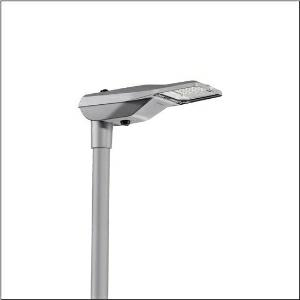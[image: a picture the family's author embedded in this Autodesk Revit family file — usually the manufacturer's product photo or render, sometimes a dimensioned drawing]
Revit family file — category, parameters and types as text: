
# Revit family: streetlight_sl_21_iq_micro___st1_0a_5xe1d31y08db_0307
name_source: partatom
category: Lighting Fixtures
units: mm (PartAtom-declared; Revit-internal decimal feet)

## family parameters
Cut with Voids When Loaded = No
Host = Face
Light Source = No
Part Type = Normal
Room Calculation Point = No
Round Connector Dimension = Use Diameter
Shared = No

## types (1)
- --- (1 x LED, 5110 lm, 39.1 W, 3000K)
    Apparent Load = 39 VA
    CIE Flux Codes = 37 72 97 100 100
    Color Rendering = 70
    Color Temperature = 3000K
    Default Elevation = 1800 mm
    Description = Streetlight SL 21 iQ micro, mast luminaire, primary light control with lens, of PMMA, primary optical cover: cover, of toughened safety glass, transparent, light distribution: ST1.0a, light emission: direct distribution, primary light characteristic: asymmetric, installation type: post-top, side-entry, LED, High Power LED, rated luminous flux: 5.110lm, luminous efficacy: 131lm/W, light colour: 730, colour temperature: 3000K, control gear: iQ-Street Remote, D4i with power reduction, control: pre-setting: logarithmic dimming characteristic, Street-Remote, Auto-Match, Temp-Guard, Lumen-Switch, Night-Set, Smart-Wire, Light-Fading, Desk-Remote (wireless, voltage-free reading and setting of iQ features in the workshop via application-optimized NFC function/RFID function), optimised constant luminous flux control (CLO 2.0), mains connection: 220..240V, AC, 50/60Hz, start of lifetime: 39W, end of service life: 41W, reduction: 17W, luminaire housing, of diecast aluminium, powder-coated, SITECO metallic grey (DB 702S), corrosivity category C5 high according to DIN EN ISO 12944, please order mast flange separately, inclination adjustable: 0°, 5°, 10°, 15°, sealing non-destructively replaceable, multi-level sealing system, length: 528mm, width: 235mm, height: 110mm, mast flange for spigot size: 42mm (side-entry): 5XC10008XM4, 60/48mm (side-entry/post-top): 5XC10108XM2, 76/60mm (side-entry/post-top): 5XC10108XM1, mounting height: 4..8m, Smart Interface below and above, protection rating (complete): IP66, insulation class (complete): insulation class II (safety insulation), certification: CE, ENEC, ENEC+, VDE, impact resistance: IK10, permissible operating ambient temperature for outdoor applications: -40..+50°C, standard-compliant lighting for roads and squares, packaging unit: 1 piece

Light Distribution: ST1.0a
    Height = 110 mm
    Lamp = 1 x LED
    Lamp Light Flux = 5110 lm
    Lamp Power = 39.1 W
    Lamp count = 1
    Length = 528 mm
    Luminous efficacy = 131 lm/W
    Manufacturer = Siteco
    ModVariant = No
    Model = 5XE1D31Y08DB
    Number of Poles = 1
    OnlyDefault = Yes
    Power Factor = 1
    Product Name = Streetlight SL 21 iQ micro | ST1.0a
    Product group = mast luminaire | pylon top
    ProductGroupID = 6100
    Protection Class = Protection class II
    Protection Degree = IP 66
    RLX_Detail_Level = 1
    RLX_Emergency_Light_Flux = 0 lm
    RLX_Emergency_Type = 0
    RLX_Emergency_Type_DB = No
    RlxData = <blob elided: 98385 chars, md5=cbb7cdfd>
    Socket = socket
    Standby Power = 0 W
    System Light Flux = 5110 lm
    System Power = 39 W
    Type Comments = factory setting: luminous flux: 100 % | dim-lin: 254 | 765 mA
    Type Image = l_1007239.jpg
    URL = http://relux.com
    VarID = @adj_115541
    Voltage = 0 V
    Weight = 0.00 kg
    Width = 235 mm

## geometry (parser evidence)
native form markers: Blend x4, Sweep x10
no freeform markers — native parametric forms only
